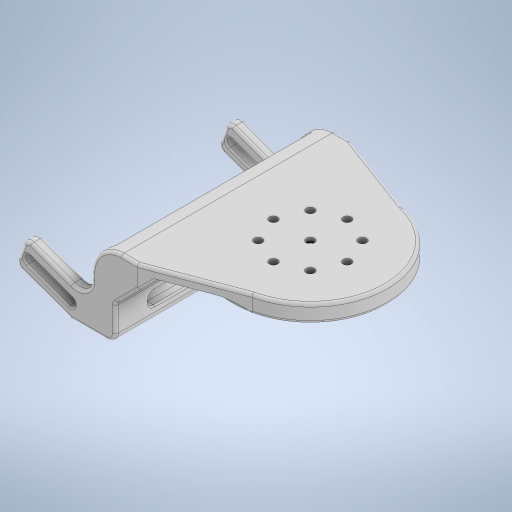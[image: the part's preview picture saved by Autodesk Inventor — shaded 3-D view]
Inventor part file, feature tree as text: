
AUTODESK INVENTOR PART (.ipt)
format: ipt  version: 2023 (Build 270158000, 158)  size: 677,888 bytes
history: native  units: mm
features: sketch x12, extrude x10, fillet x10, chamfer x2, hole x2, plane x1
ambient origin geometry x8: Origin, YZ Plane, XZ Plane, XY Plane, X Axis, Y Axis, Z Axis, Center Point
bodies: Volumenkörper1 (feature_tree)
feature tree (37):
  extrude  "Extrusion1"  Depth=6.0mm
  chamfer  "Fase1"  Distance=6.0mm
  extrude  "Extrusion2"  Depth=6.0mm TaperAngle=0.0deg
  hole  "Bohrung1"  [1 undecoded]
  hole  "Bohrung2"  [1 undecoded]
  extrude  "Extrusion3"  Depth=6.0mm
  extrude  "Extrusion8"  Depth=6.0mm
  extrude  "Extrusion9"  Depth=27.925268mm
  extrude  "Extrusion10"  Depth=55.0mm
  plane  "Arbeitsebene1"
  extrude  "Extrusion11"  Depth=115.0mm TaperAngle=0.0deg
  extrude  "Extrusion12"  Depth=8.0mm TaperAngle=0.0deg
  extrude  "Extrusion13"  Depth=100.0mm
  extrude  "Extrusion14"  Depth=10.0mm TaperAngle=0.0deg
  fillet  "Rundung21"  Radius=10.0mm
  fillet  "Rundung22"  [1 undecoded]
  fillet  "Rundung23"  [1 undecoded]
  chamfer  "Fase6"  Distance=145.0mm
  fillet  "Rundung24"  Radius=72.5mm
  fillet  "Rundung25"  Radius=15.0mm
  fillet  "Rundung26"  Radius=15.0mm
  fillet  "Rundung27"  Radius=10.0mm
  fillet  "Rundung28"  Radius=22.5mm
  fillet  "Rundung29"  Radius=6.5mm
  fillet  "Rundung30"  Radius=6.5mm
  sketch  "Skizze1"  dims[d0=66.0mm d1=105.0mm d2=6.0mm d3=0.0mm]
  sketch  "Skizze2"  dims[d4=2.0mm d5=2.0mm d6=45.0deg d9=6.0mm d10=0.0mm]
  sketch  "Skizze3"  dims[d11=5.5mm d12=6.0mm d13=4.0mm d14=2.0mm d15=90.0deg d16=15.0mm d17=20.594885mm d18=50.0mm]
  sketch  "Skizze5"  dims[d19=80.0mm d21=360.0deg]
  sketch  "Skizze6"  dims[d26=5.5mm d27=6.0mm d28=13.0mm d29=2.0mm d30=90.0deg d31=15.0mm d32=20.594885mm d35=60.0mm]
  sketch  "Skizze12"  dims[d36=6.0mm d37=0.0mm d79=6.0mm]
  sketch  "Skizze13"  dims[d80=6.0mm d81=6.0mm]
  sketch  "Skizze14"  dims[d82=30.0mm d83=27.925268mm]
  sketch  "Skizze15"  dims[d84=40.0mm d85=55.0mm]
  sketch  "Skizze16"  dims[d86=145.0mm d87=0.0mm d88=115.0mm d89=0.0mm]
  sketch  "Skizze17"  dims[d91=8.0mm d92=0.0mm d93=8.0mm d94=0.0mm]
  sketch  "Skizze18"  dims[d95=9.0mm d96=100.0mm d99=20.0mm d100=0.0mm d101=10.0mm d102=0.0mm d105=0.0mm d106=0.0mm d115=0.0mm d116=0.0mm d146=145.0mm d147=72.5mm d148=15.0mm d149=15.0mm d150=10.0mm d151=22.5mm d152=6.5mm d153=6.5mm d154=30.0mm d155=6.0mm d156=6.0mm d157=20.0mm d158=10.0mm d159=10.0mm d160=20.0mm d161=4.0mm d162=1.0mm d163=25.0mm d164=2.0mm d165=45.0deg d166=6.0mm d167=3.0mm d168=3.0mm d169=6.0mm d170=2.0mm d171=4.0mm d172=1.0mm d173=10.0mm d33=0.75mm d34=20.594885mm d97=0.0mm d98=0.0mm d138=0.0mm d139=0.0mm d140=0.0mm d141=0.0mm d145=0.5mm]
note: 4 required parameter values undecoded (feature->parameter linkage not recoverable at this tier; creation-order binding heuristic only, values carry confidence <= 0.55)
